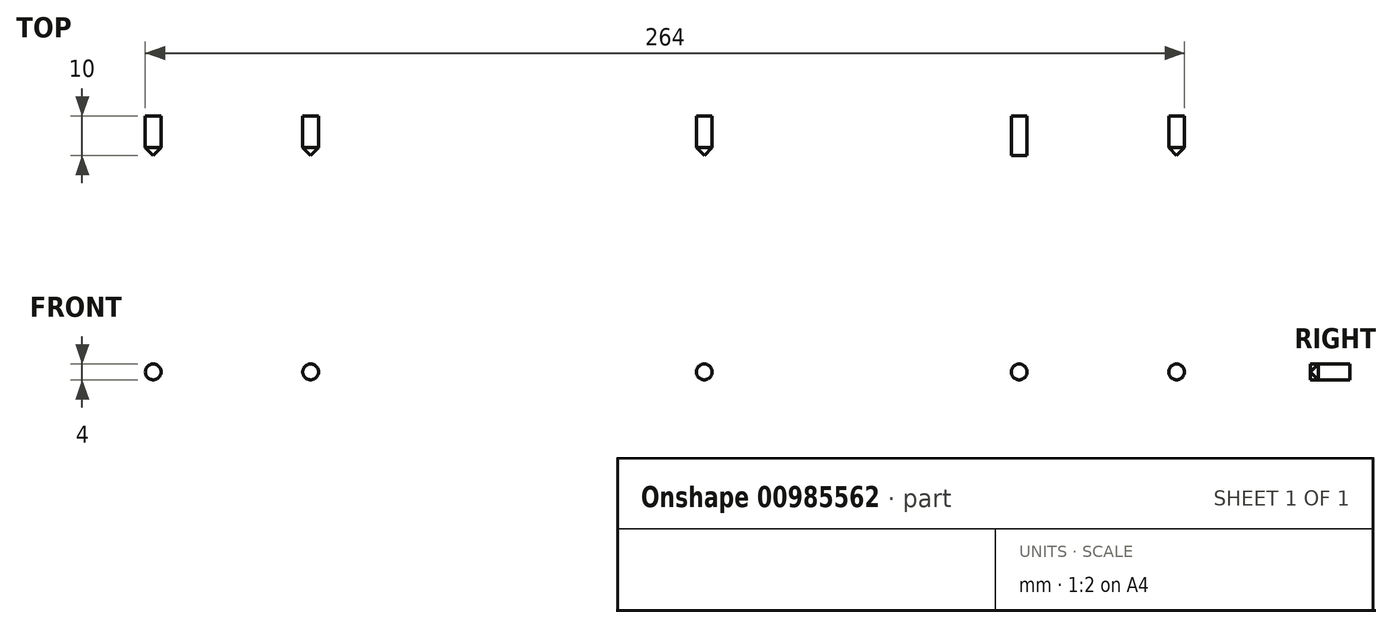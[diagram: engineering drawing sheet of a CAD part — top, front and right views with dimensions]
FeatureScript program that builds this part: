
annotation { "Feature Type Name" : "Feature", "Feature Type Description" : "" }
export const myFeature = defineFeature(function(context is Context, id is Id, definition is map)
    precondition{}
    {
        {
            var Q0;
            Q0=qCreatedBy(makeId("Front.planeOp"),FACE);
            var sketch = newSketch(context, id + "F0", { "sketchPlane" : qUnion([Q0])});
            skLineSegment(sketch, "E0.bottom", {"start": v(173, -25) * mm, "end": v(-173, -25) * mm});
            skLineSegment(sketch, "E0.top", {"start": v(173, 25) * mm, "end": v(-173, 25) * mm});
            skLineSegment(sketch, "E0.left", {"start": v(173, -25) * mm, "end": v(173, 25) * mm});
            skLineSegment(sketch, "E0.right", {"start": v(-173, -25) * mm, "end": v(-173, 25) * mm});
            skPoint(sketch, "E0.middle", {"position": v(0, 0) * mm});
            skSolve(sketch);
        }
        {
            var Q0;
            Q0 = qSketchRegion(id + "F0", true);
            extrude(context, id + "F1", {"entities" : qUnion([Q0]), "depth" : 10 * mm, "offsetDistance" : 25.4 * mm});
        }
        {
            var Q0;
            Q0=makeQuery(id+"F1.opExtrude","CAP_FACE",FACE,{"disambiguationData":[OSD([sQuery(id+"F0.wireOp",EDGE,"E0.bottom"),sQuery(id+"F0.wireOp",EDGE,"E0.top"),sQuery(id+"F0.wireOp",EDGE,"E0.left"),sQuery(id+"F0.wireOp",EDGE,"E0.right")])],"isStart":false});
            var sketch = newSketch(context, id + "F2", { "sketchPlane" : qUnion([Q0])});
            skLineSegment(sketch, "E1", {"start": v(-317.4, -5) * mm, "end": v(328.54, -5) * mm});
            skLineSegment(sketch, "E2", {"start": v(0, 49.7) * mm, "end": v(0, -53.62) * mm});
            skPoint(sketch, "E2.startSnap0", {"position": v(0, 25) * mm});
            skCircle(sketch, "E3", {"center": v(-150, -5) * mm, "radius": 2 * mm});
            skCircle(sketch, "E4", {"center": v(-110, -5) * mm, "radius": 2 * mm});
            skCircle(sketch, "E5", {"center": v(-70, -5) * mm, "radius": 2 * mm});
            skCircle(sketch, "E6", {"center": v(-30, -5) * mm, "radius": 2 * mm});
            skCircle(sketch, "E7", {"center": v(30, -5) * mm, "radius": 2 * mm});
            skCircle(sketch, "E8", {"center": v(70, -5) * mm, "radius": 2 * mm});
            skCircle(sketch, "E9", {"center": v(110, -5) * mm, "radius": 2 * mm});
            skCircle(sketch, "E10", {"center": v(150, -5) * mm, "radius": 2 * mm});
            skSolve(sketch);
        }
        {
            var Q0;
            {var subQ0=sQuery(id+"F2.wireOp",EDGE,"E3");var subQ1=sQuery(id+"F2.wireOp",EDGE,"E1");var subQ2=makeQuery(id+"F2.imprint","INTERSECT",VERTEX,{"disambiguationData":[OD(0.0)],"derivedFrom":[subQ1,subQ0]});Q0=makeQuery(id+"F2.imprint","IMPRINT",FACE,{"disambiguationData":[TD([[makeQuery(id+"F2.imprint","IMPRINT",EDGE,{"disambiguationData":[TD([[subQ2,-1.0]])],"derivedFrom":subQ1}),1.0]])]});}
            var Q1;
            {var subQ0=sQuery(id+"F2.wireOp",EDGE,"E3");var subQ1=sQuery(id+"F2.wireOp",EDGE,"E1");var subQ2=makeQuery(id+"F2.imprint","INTERSECT",VERTEX,{"disambiguationData":[OD(0.0)],"derivedFrom":[subQ1,subQ0]});Q1=makeQuery(id+"F2.imprint","IMPRINT",FACE,{"disambiguationData":[TD([[makeQuery(id+"F2.imprint","IMPRINT",EDGE,{"disambiguationData":[TD([[subQ2,-1.0]])],"derivedFrom":subQ1}),-1.0]])]});}
            var Q2;
            {var subQ0=sQuery(id+"F2.wireOp",EDGE,"E4");var subQ1=sQuery(id+"F2.wireOp",EDGE,"E1");var subQ2=makeQuery(id+"F2.imprint","INTERSECT",VERTEX,{"disambiguationData":[OD(0.0)],"derivedFrom":[subQ1,subQ0]});Q2=makeQuery(id+"F2.imprint","IMPRINT",FACE,{"disambiguationData":[TD([[makeQuery(id+"F2.imprint","IMPRINT",EDGE,{"disambiguationData":[TD([[subQ2,-1.0]])],"derivedFrom":subQ1}),1.0]])]});}
            var Q3;
            {var subQ0=sQuery(id+"F2.wireOp",EDGE,"E4");var subQ1=sQuery(id+"F2.wireOp",EDGE,"E1");var subQ2=makeQuery(id+"F2.imprint","INTERSECT",VERTEX,{"disambiguationData":[OD(0.0)],"derivedFrom":[subQ1,subQ0]});Q3=makeQuery(id+"F2.imprint","IMPRINT",FACE,{"disambiguationData":[TD([[makeQuery(id+"F2.imprint","IMPRINT",EDGE,{"disambiguationData":[TD([[subQ2,-1.0]])],"derivedFrom":subQ1}),-1.0]])]});}
            var Q4;
            {var subQ0=sQuery(id+"F2.wireOp",EDGE,"E5");var subQ1=sQuery(id+"F2.wireOp",EDGE,"E1");var subQ2=makeQuery(id+"F2.imprint","INTERSECT",VERTEX,{"disambiguationData":[OD(0.0)],"derivedFrom":[subQ1,subQ0]});Q4=makeQuery(id+"F2.imprint","IMPRINT",FACE,{"disambiguationData":[TD([[makeQuery(id+"F2.imprint","IMPRINT",EDGE,{"disambiguationData":[TD([[subQ2,-1.0]])],"derivedFrom":subQ1}),1.0]])]});}
            var Q5;
            {var subQ0=sQuery(id+"F2.wireOp",EDGE,"E5");var subQ1=sQuery(id+"F2.wireOp",EDGE,"E1");var subQ2=makeQuery(id+"F2.imprint","INTERSECT",VERTEX,{"disambiguationData":[OD(0.0)],"derivedFrom":[subQ1,subQ0]});Q5=makeQuery(id+"F2.imprint","IMPRINT",FACE,{"disambiguationData":[TD([[makeQuery(id+"F2.imprint","IMPRINT",EDGE,{"disambiguationData":[TD([[subQ2,-1.0]])],"derivedFrom":subQ1}),-1.0]])]});}
            var Q6;
            {var subQ0=sQuery(id+"F2.wireOp",EDGE,"E6");var subQ1=sQuery(id+"F2.wireOp",EDGE,"E1");var subQ2=makeQuery(id+"F2.imprint","INTERSECT",VERTEX,{"disambiguationData":[OD(0.0)],"derivedFrom":[subQ1,subQ0]});Q6=makeQuery(id+"F2.imprint","IMPRINT",FACE,{"disambiguationData":[TD([[makeQuery(id+"F2.imprint","IMPRINT",EDGE,{"disambiguationData":[TD([[subQ2,-1.0]])],"derivedFrom":subQ1}),1.0]])]});}
            var Q7;
            {var subQ0=sQuery(id+"F2.wireOp",EDGE,"E6");var subQ1=sQuery(id+"F2.wireOp",EDGE,"E1");var subQ2=makeQuery(id+"F2.imprint","INTERSECT",VERTEX,{"disambiguationData":[OD(0.0)],"derivedFrom":[subQ1,subQ0]});Q7=makeQuery(id+"F2.imprint","IMPRINT",FACE,{"disambiguationData":[TD([[makeQuery(id+"F2.imprint","IMPRINT",EDGE,{"disambiguationData":[TD([[subQ2,-1.0]])],"derivedFrom":subQ1}),-1.0]])]});}
            var Q8;
            {var subQ0=sQuery(id+"F2.wireOp",EDGE,"E7");var subQ1=sQuery(id+"F2.wireOp",EDGE,"E1");var subQ2=makeQuery(id+"F2.imprint","INTERSECT",VERTEX,{"disambiguationData":[OD(0.0)],"derivedFrom":[subQ1,subQ0]});Q8=makeQuery(id+"F2.imprint","IMPRINT",FACE,{"disambiguationData":[TD([[makeQuery(id+"F2.imprint","IMPRINT",EDGE,{"disambiguationData":[TD([[subQ2,-1.0]])],"derivedFrom":subQ1}),1.0]])]});}
            var Q9;
            {var subQ0=sQuery(id+"F2.wireOp",EDGE,"E7");var subQ1=sQuery(id+"F2.wireOp",EDGE,"E1");var subQ2=makeQuery(id+"F2.imprint","INTERSECT",VERTEX,{"disambiguationData":[OD(0.0)],"derivedFrom":[subQ1,subQ0]});Q9=makeQuery(id+"F2.imprint","IMPRINT",FACE,{"disambiguationData":[TD([[makeQuery(id+"F2.imprint","IMPRINT",EDGE,{"disambiguationData":[TD([[subQ2,-1.0]])],"derivedFrom":subQ1}),-1.0]])]});}
            var Q10;
            {var subQ0=sQuery(id+"F2.wireOp",EDGE,"E8");var subQ1=sQuery(id+"F2.wireOp",EDGE,"E1");var subQ2=makeQuery(id+"F2.imprint","INTERSECT",VERTEX,{"disambiguationData":[OD(0.0)],"derivedFrom":[subQ1,subQ0]});Q10=makeQuery(id+"F2.imprint","IMPRINT",FACE,{"disambiguationData":[TD([[makeQuery(id+"F2.imprint","IMPRINT",EDGE,{"disambiguationData":[TD([[subQ2,-1.0]])],"derivedFrom":subQ1}),1.0]])]});}
            var Q11;
            {var subQ0=sQuery(id+"F2.wireOp",EDGE,"E8");var subQ1=sQuery(id+"F2.wireOp",EDGE,"E1");var subQ2=makeQuery(id+"F2.imprint","INTERSECT",VERTEX,{"disambiguationData":[OD(0.0)],"derivedFrom":[subQ1,subQ0]});Q11=makeQuery(id+"F2.imprint","IMPRINT",FACE,{"disambiguationData":[TD([[makeQuery(id+"F2.imprint","IMPRINT",EDGE,{"disambiguationData":[TD([[subQ2,-1.0]])],"derivedFrom":subQ1}),-1.0]])]});}
            var Q12;
            {var subQ0=sQuery(id+"F2.wireOp",EDGE,"E9");var subQ1=sQuery(id+"F2.wireOp",EDGE,"E1");var subQ2=makeQuery(id+"F2.imprint","INTERSECT",VERTEX,{"disambiguationData":[OD(0.0)],"derivedFrom":[subQ1,subQ0]});Q12=makeQuery(id+"F2.imprint","IMPRINT",FACE,{"disambiguationData":[TD([[makeQuery(id+"F2.imprint","IMPRINT",EDGE,{"disambiguationData":[TD([[subQ2,-1.0]])],"derivedFrom":subQ1}),1.0]])]});}
            var Q13;
            {var subQ0=sQuery(id+"F2.wireOp",EDGE,"E9");var subQ1=sQuery(id+"F2.wireOp",EDGE,"E1");var subQ2=makeQuery(id+"F2.imprint","INTERSECT",VERTEX,{"disambiguationData":[OD(0.0)],"derivedFrom":[subQ1,subQ0]});Q13=makeQuery(id+"F2.imprint","IMPRINT",FACE,{"disambiguationData":[TD([[makeQuery(id+"F2.imprint","IMPRINT",EDGE,{"disambiguationData":[TD([[subQ2,-1.0]])],"derivedFrom":subQ1}),-1.0]])]});}
            var Q14;
            {var subQ0=sQuery(id+"F2.wireOp",EDGE,"E10");var subQ1=sQuery(id+"F2.wireOp",EDGE,"E1");var subQ2=makeQuery(id+"F2.imprint","INTERSECT",VERTEX,{"disambiguationData":[OD(0.0)],"derivedFrom":[subQ1,subQ0]});Q14=makeQuery(id+"F2.imprint","IMPRINT",FACE,{"disambiguationData":[TD([[makeQuery(id+"F2.imprint","IMPRINT",EDGE,{"disambiguationData":[TD([[subQ2,-1.0]])],"derivedFrom":subQ1}),1.0]])]});}
            var Q15;
            {var subQ0=sQuery(id+"F2.wireOp",EDGE,"E10");var subQ1=sQuery(id+"F2.wireOp",EDGE,"E1");var subQ2=makeQuery(id+"F2.imprint","INTERSECT",VERTEX,{"disambiguationData":[OD(0.0)],"derivedFrom":[subQ1,subQ0]});Q15=makeQuery(id+"F2.imprint","IMPRINT",FACE,{"disambiguationData":[TD([[makeQuery(id+"F2.imprint","IMPRINT",EDGE,{"disambiguationData":[TD([[subQ2,-1.0]])],"derivedFrom":subQ1}),-1.0]])]});}
            extrude(context, id + "F3", {"entities" : qUnion([Q0, Q1, Q2, Q3, Q4, Q5, Q6, Q7, Q8, Q9, Q10, Q11, Q12, Q13, Q14, Q15]), "operationType" : NewBodyOperationType.REMOVE, "endBound" : BoundingType.THROUGH_ALL, "oppositeDirection" : true, "depth" : 25.4 * mm, "offsetDistance" : 25.4 * mm});
        }
        {
            var Q0;
            Q0=makeQuery(id+"F3.boolean.opBoolean","COPY",EDGE,{"derivedFrom":makeQuery(id+"F3.opExtrude","CAP_EDGE",EDGE,{"disambiguationData":[OSD([sQuery(id+"F2.wireOp",EDGE,"E3")])],"isStart":true})});
            var Q1;
            Q1=makeQuery(id+"F3.boolean.opBoolean","COPY",EDGE,{"derivedFrom":makeQuery(id+"F3.opExtrude","CAP_EDGE",EDGE,{"disambiguationData":[OSD([sQuery(id+"F2.wireOp",EDGE,"E4")])],"isStart":true})});
            var Q2;
            Q2=makeQuery(id+"F3.boolean.opBoolean","COPY",EDGE,{"derivedFrom":makeQuery(id+"F3.opExtrude","CAP_EDGE",EDGE,{"disambiguationData":[OSD([sQuery(id+"F2.wireOp",EDGE,"E5")])],"isStart":true})});
            var Q3;
            Q3=makeQuery(id+"F3.boolean.opBoolean","COPY",EDGE,{"derivedFrom":makeQuery(id+"F3.opExtrude","CAP_EDGE",EDGE,{"disambiguationData":[OSD([sQuery(id+"F2.wireOp",EDGE,"E6")])],"isStart":true})});
            var Q4;
            Q4=makeQuery(id+"F3.boolean.opBoolean","COPY",EDGE,{"derivedFrom":makeQuery(id+"F3.opExtrude","CAP_EDGE",EDGE,{"disambiguationData":[OSD([sQuery(id+"F2.wireOp",EDGE,"E7")])],"isStart":true})});
            var Q5;
            Q5=makeQuery(id+"F3.boolean.opBoolean","COPY",EDGE,{"derivedFrom":makeQuery(id+"F3.opExtrude","CAP_EDGE",EDGE,{"disambiguationData":[OSD([sQuery(id+"F2.wireOp",EDGE,"E8")])],"isStart":true})});
            var Q6;
            Q6=makeQuery(id+"F3.boolean.opBoolean","COPY",EDGE,{"derivedFrom":makeQuery(id+"F3.opExtrude","CAP_EDGE",EDGE,{"disambiguationData":[OSD([sQuery(id+"F2.wireOp",EDGE,"E9")])],"isStart":true})});
            var Q7;
            Q7=makeQuery(id+"F3.boolean.opBoolean","COPY",EDGE,{"derivedFrom":makeQuery(id+"F3.opExtrude","CAP_EDGE",EDGE,{"disambiguationData":[OSD([sQuery(id+"F2.wireOp",EDGE,"E10")])],"isStart":true})});
            chamfer(context, id + "F4", {"entities" : qUnion([Q0, Q1, Q2, Q3, Q4, Q5, Q6, Q7]), "width" : 2 * mm, "tangentPropagation" : true});
        }
    });
